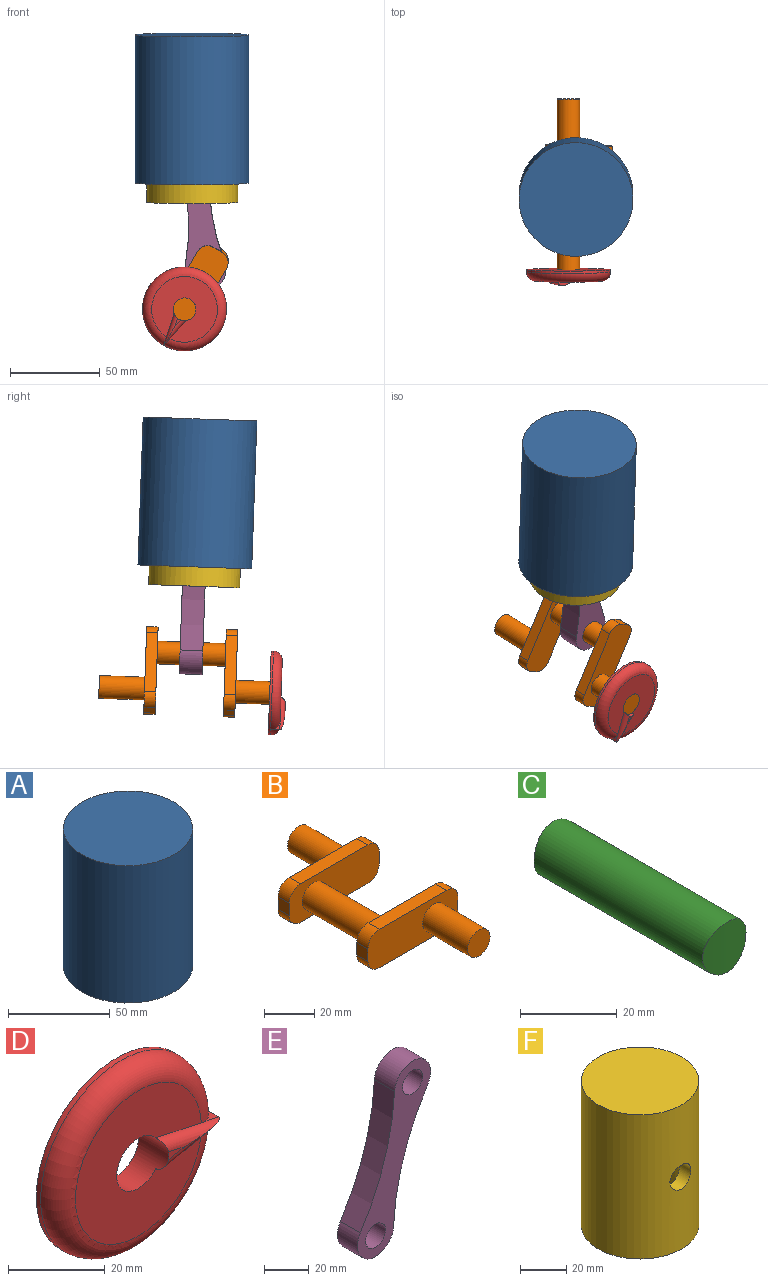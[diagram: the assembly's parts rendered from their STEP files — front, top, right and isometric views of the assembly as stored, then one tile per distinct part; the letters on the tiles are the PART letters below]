
ASSEMBLY  parts=6 mates=5
PART A: 5 faces, bbox 63.5x63.5x82.6 mm
  f0: plane 50.8x50.8mm, normal (0,0,-1), area 2026.8mm2, adj f4
  f1: plane 63.5x63.5mm, normal (0,0,1), area 3166.9mm2, adj f2
  f2: cylinder r=31.75mm len=82.55mm, axis (0,0,-1), area 16468mm2, adj f1,f3
  f3: plane 63.5x63.5mm, normal (0,0,-1), area 1140.1mm2, adj f2,f4
  f4: cylinder r=25.4mm len=76.2mm, axis (0,0,-1), area 12161mm2, adj f0,f3
PART B: 25 faces, bbox 50.8x101.6x18.8 mm
  f0: cylinder r=6.35mm len=38.1mm, axis (0,1,0), area 1520.1mm2, adj f9,f21
  f1: plane 6.35x6.1mm, normal (-1,0,0), area 38.7mm2, adj f2,f8,f9,f10
  f2: cylinder r=6.35mm len=6.35mm, axis (0,-1,0), area 63.3mm2, adj f1,f3,f9,f10
  f3: plane 38.1x6.35mm, normal (0,0,-1), area 241.9mm2, adj f2,f4,f9,f10
  f4: cylinder r=6.35mm len=6.35mm, axis (0,-1,0), area 63.3mm2, adj f3,f5,f9,f10
  f5: plane 6.35x6.1mm, normal (1,0,0), area 38.7mm2, adj f4,f6,f9,f10
  f6: cylinder r=6.35mm len=6.35mm, axis (0,-1,0), area 63.3mm2, adj f5,f7,f9,f10
  f7: plane 38.1x6.35mm, normal (0,0,1), area 241.9mm2, adj f6,f8,f9,f10
  f8: cylinder r=6.35mm len=6.35mm, axis (0,-1,0), area 63.3mm2, adj f1,f7,f9,f10
  f9: plane 50.8x18.8mm, normal (0,1,0), area 793.5mm2, adj f0,f1,f2,f3,f4,f5,f6,f7
  f10: plane 50.8x18.8mm, normal (0,-1,0), area 793.5mm2, adj f1,f2,f3,f4,f5,f6,f7,f8
  f11: plane 12.7x12.7mm, normal (0,-1,0), area 126.7mm2, adj f12
  f12: cylinder r=6.35mm len=25.4mm, axis (0,-1,0), area 1013.4mm2, adj f10,f11
  f13: plane 6.35x6.1mm, normal (-1,0,0), area 38.7mm2, adj f14,f20,f21,f22
  f14: cylinder r=6.35mm len=6.35mm, axis (0,1,0), area 63.3mm2, adj f13,f15,f21,f22
  f15: plane 38.1x6.35mm, normal (0,0,1), area 241.9mm2, adj f14,f16,f21,f22
  f16: cylinder r=6.35mm len=6.35mm, axis (0,1,0), area 63.3mm2, adj f15,f17,f21,f22
  f17: plane 6.35x6.1mm, normal (1,0,0), area 38.7mm2, adj f16,f18,f21,f22
  f18: cylinder r=6.35mm len=6.35mm, axis (0,1,0), area 63.3mm2, adj f17,f19,f21,f22
  f19: plane 38.1x6.35mm, normal (0,0,-1), area 241.9mm2, adj f18,f20,f21,f22
  f20: cylinder r=6.35mm len=6.35mm, axis (0,1,0), area 63.3mm2, adj f13,f19,f21,f22
  f21: plane 50.8x18.8mm, normal (0,-1,0), area 793.5mm2, adj f0,f13,f14,f15,f16,f17,f18,f19
  f22: plane 50.8x18.8mm, normal (0,1,0), area 793.5mm2, adj f13,f14,f15,f16,f17,f18,f19,f20
  f23: plane 12.7x12.7mm, normal (0,1,0), area 126.7mm2, adj f24
  f24: cylinder r=6.35mm len=25.4mm, axis (0,1,0), area 1013.4mm2, adj f22,f23
PART C: 3 faces, bbox 12.7x50.8x12.7 mm
  f0: cylinder r=25.4mm len=12.7mm, axis (0,0,1), area 127.7mm2, adj f2
  f1: cylinder r=25.4mm len=12.7mm, axis (0,0,1), area 127.7mm2, adj f2
  f2: cylinder r=6.35mm len=50.8mm, axis (0,1,0), area 1994.8mm2, adj f0,f1
PART D: 10 faces, bbox 50.7x8.9x50.7 mm
  f0: cylinder r=23.43mm len=46.87mm, axis (0,-1,0), area 187mm2, adj f2,f7
  f1: cylinder r=6.35mm len=12.7mm, axis (0,-1,0), area 270.7mm2, adj f2,f3,f6,f8,f9
  f2: plane 46.87x46.87mm, normal (0,1,0), area 1598.5mm2, adj f0,f1
  f3: plane 36.71x36.68mm, normal (0,-1,0), area 872.9mm2, adj f1,f7,f8,f9
  f4: plane 5.11x5.08mm, normal (0.21,0,-0.98), area 5.7mm2, adj f5,f7,f9
  f5: plane 5.11x5.08mm, normal (0.21,0,0.98), area 5.7mm2, adj f4,f7,f8
  f6: plane 4.8x2.02mm, normal (0,-1,0), area 4.7mm2, adj f1,f8,f9
  f7: torus R=18.35mm, axis (0,-1,0), area 1076.1mm2, adj f0,f3,f4,f5
  f8: cylinder r=2.54mm len=18.92mm, axis (0.98,0,-0.21), area 54.3mm2, adj f1,f3,f5,f6,f9
  f9: cylinder r=2.54mm len=18.92mm, axis (-0.98,0,-0.21), area 54.3mm2, adj f1,f3,f4,f6,f8
PART E: 8 faces, bbox 46.3x12.7x95.4 mm
  f0: cylinder r=133.98mm len=66.81mm, axis (0,1,0), area 902.2mm2, adj f1,f5,f6,f7
  f1: cylinder r=11.43mm len=22.85mm, axis (0,1,0), area 533mm2, adj f0,f2,f6,f7
  f2: cylinder r=133.98mm len=66.81mm, axis (0,1,0), area 902.2mm2, adj f1,f5,f6,f7
  f3: cylinder r=6.35mm len=12.7mm, axis (0,1,0), area 506.7mm2, adj f6,f7
  f4: cylinder r=6.35mm len=12.7mm, axis (0,1,0), area 506.7mm2, adj f6,f7
  f5: cylinder r=11.43mm len=22.85mm, axis (0,1,0), area 533mm2, adj f0,f2,f6,f7
  f6: plane 95.37x46.29mm, normal (0,-1,0), area 1401.6mm2, adj f0,f1,f2,f3,f4,f5
  f7: plane 95.37x46.29mm, normal (0,1,0), area 1401.6mm2, adj f0,f1,f2,f3,f4,f5
PART F: 7 faces, bbox 50.8x50.8x76.2 mm
  f0: cylinder r=25.4mm len=76.2mm, axis (0,0,1), area 11905.2mm2, adj f1,f4,f5,f6
  f1: plane 50.8x50.8mm, normal (0,0,-1), area 886.7mm2, adj f0,f2
  f2: cylinder r=19.05mm len=69.85mm, axis (0,0,1), area 8103.4mm2, adj f1,f3,f5,f6
  f3: plane 38.1x38.1mm, normal (0,0,-1), area 1140.1mm2, adj f2
  f4: plane 50.8x50.8mm, normal (0,0,1), area 2026.8mm2, adj f0
  f5: cylinder r=6.35mm len=12.7mm, axis (0,-1,0), area 258.9mm2, adj f0,f2
  f6: cylinder r=6.35mm len=12.7mm, axis (0,-1,0), area 258.9mm2, adj f0,f2
PLACE A rot(axis=(1,0,0),2deg) t=(30.64,-26.21,-81.74)mm fixed
PLACE B rot(axis=(0.01,1,0.02),119.9deg) t=(56.3,-22.95,-167.6)mm
PLACE C rot(axis=(1,0,0),2deg) t=(30.64,-25.58,-92.46)mm
PLACE D rot(axis=(0.01,1,0.02),119.9deg) t=(56.3,-22.95,-167.6)mm
PLACE E rot(axis=(0.08,-1,-0.02),23.6deg) t=(45.86,-25.69,-89.3)mm
PLACE F rot(axis=(1,0,0),2deg) t=(30.64,-25.84,-92.47)mm
MATE slider F.f0 <-> A.f2  axis (0,-0.03,1) through (30.64,-27.17,-54.4)mm
MATE revolute E.f3 <-> B.f0  axis (0,1,0.03) through (38.12,-24.26,-130.17)mm
MATE fastened D.f0 <-> B.f12  axis (0,-1,-0.03) through (26.45,-74.32,-152.26)mm
MATE revolute E.f4 <-> C.f2  axis (0,1,0.03) through (30.64,-26.91,-54.39)mm
MATE fastened F.f5 <-> C.f2  axis (0,-1,-0.03) through (30.64,-52.61,-55.29)mm
